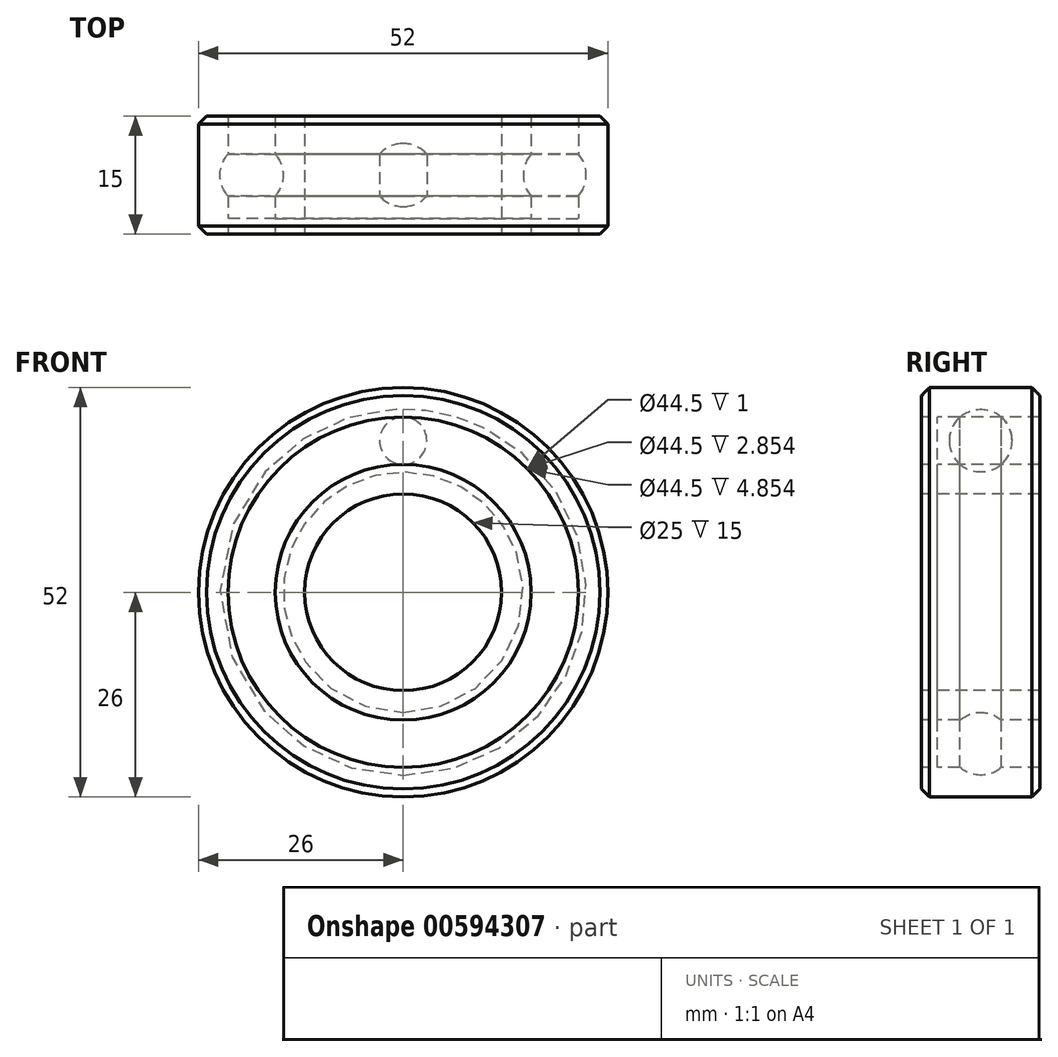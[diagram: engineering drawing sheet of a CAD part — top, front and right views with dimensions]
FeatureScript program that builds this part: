
annotation { "Feature Type Name" : "Feature", "Feature Type Description" : "" }
export const myFeature = defineFeature(function(context is Context, id is Id, definition is map)
    precondition{}
    {
        {
            var Q0;
            Q0=qCreatedBy(makeId("Right.planeOp"),FACE);
            var sketch = newSketch(context, id + "F0", { "sketchPlane" : qUnion([Q0])});
            skLineSegment(sketch, "E0", {"start": v(-30, 0) * mm, "end": v(30, 0) * mm, "construction": true});
            skSolve(sketch);
        }
        {
            var Q0;
            Q0=qCreatedBy(makeId("Right.planeOp"),FACE);
            var sketch = newSketch(context, id + "F1", { "sketchPlane" : qUnion([Q0])});
            skLineSegment(sketch, "E1.bottom", {"start": v(-7.5, 26) * mm, "end": v(7.5, 26) * mm});
            skLineSegment(sketch, "E1.top", {"start": v(-7.5, 12.5) * mm, "end": v(7.5, 12.5) * mm});
            skLineSegment(sketch, "E1.left", {"start": v(-7.5, 26) * mm, "end": v(-7.5, 12.5) * mm});
            skLineSegment(sketch, "E1.right", {"start": v(7.5, 26) * mm, "end": v(7.5, 12.5) * mm});
            skLineSegment(sketch, "E2", {"start": v(-11.72, 19.25) * mm, "end": v(12.7, 19.25) * mm, "construction": true});
            skCircle(sketch, "E3", {"center": v(0, 19.25) * mm, "radius": 4 * mm});
            skLineSegment(sketch, "E4", {"start": v(-7.5, 22.25) * mm, "end": v(7.5, 22.25) * mm});
            skLineSegment(sketch, "E5", {"start": v(-7.5, 16.25) * mm, "end": v(7.5, 16.25) * mm});
            skLineSegment(sketch, "E6.bottom", {"start": v(-6.5, 23.25) * mm, "end": v(-5.5, 23.25) * mm});
            skLineSegment(sketch, "E6.top", {"start": v(-6.5, 15.25) * mm, "end": v(-5.5, 15.25) * mm});
            skLineSegment(sketch, "E6.left", {"start": v(-6.5, 23.25) * mm, "end": v(-6.5, 15.25) * mm});
            skLineSegment(sketch, "E6.right", {"start": v(-5.5, 23.25) * mm, "end": v(-5.5, 15.25) * mm});
            skLineSegment(sketch, "E7", {"start": v(-4, 19.25) * mm, "end": v(4, 19.25) * mm});
            skSolve(sketch);
        }
        {
            var Q0;
            {var subQ5=sQuery(id+"F1.wireOp",EDGE,"E1.bottom");Q0=makeQuery(id+"F1.imprint","IMPRINT",FACE,{"disambiguationData":[TD([[makeQuery(id+"F1.imprint","IMPRINT",EDGE,{"derivedFrom":subQ5}),-1.0]])]});}
            var Q1;
            {var subQ4=sQuery(id+"F1.wireOp",EDGE,"E1.top");Q1=makeQuery(id+"F1.imprint","IMPRINT",FACE,{"disambiguationData":[TD([[makeQuery(id+"F1.imprint","IMPRINT",EDGE,{"derivedFrom":subQ4}),1.0]])]});}
            var Q2;
            Q2=sQuery(id+"F0.wireOp",EDGE,"E0");
            revolve(context, id + "F2", {"entities" : qUnion([Q0, Q1]), "axis" : qUnion([Q2]), "revolveType" : RevolveType.FULL});
        }
        {
            var Q0;
            Q0=makeQuery(id+"F2.opRevolve","SWEPT_EDGE",EDGE,{"disambiguationData":[OSD([sQuery(id+"F1.wireOp",EDGE,"E1.bottom"),sQuery(id+"F1.wireOp",EDGE,"E1.right")])]});
            var Q1;
            Q1=makeQuery(id+"F2.opRevolve","SWEPT_EDGE",EDGE,{"disambiguationData":[OSD([sQuery(id+"F1.wireOp",EDGE,"E1.bottom"),sQuery(id+"F1.wireOp",EDGE,"E1.left")])]});
            chamfer(context, id + "F3", {"entities" : qUnion([Q0, Q1]), "width" : 1 * mm, "tangentPropagation" : true});
        }
        {
            var Q0;
            {var subQ0=sQuery(id+"F1.wireOp",EDGE,"E7");Q0=makeQuery(id+"F1.imprint","IMPRINT",FACE,{"disambiguationData":[TD([[makeQuery(id+"F1.imprint","IMPRINT",EDGE,{"derivedFrom":subQ0}),1.0]])]});}
            var Q1;
            {var subQ0=sQuery(id+"F1.wireOp",EDGE,"E4");var subQ1=sQuery(id+"F1.wireOp",EDGE,"E3");var subQ2=makeQuery(id+"F1.imprint","INTERSECT",VERTEX,{"disambiguationData":[OD(0.0)],"derivedFrom":[subQ1,subQ0]});Q1=makeQuery(id+"F1.imprint","IMPRINT",FACE,{"disambiguationData":[TD([[makeQuery(id+"F1.imprint","IMPRINT",EDGE,{"disambiguationData":[TD([[subQ2,-1.0]])],"derivedFrom":subQ1}),1.0]])]});}
            var Q2;
            Q2=sQuery(id+"F1.wireOp",EDGE,"E2");
            revolve(context, id + "F4", {"operationType" : NewBodyOperationType.ADD, "entities" : qUnion([Q0, Q1]), "axis" : qUnion([Q2]), "revolveType" : RevolveType.FULL});
        }
        {
            var Q0;
            {var subQ5=sQuery(id+"F1.wireOp",EDGE,"E6.bottom");Q0=makeQuery(id+"F1.imprint","IMPRINT",FACE,{"disambiguationData":[TD([[makeQuery(id+"F1.imprint","IMPRINT",EDGE,{"derivedFrom":subQ5}),-1.0]])]});}
            var Q1;
            {var subQ0=sQuery(id+"F1.wireOp",EDGE,"E6.left");var subQ1=sQuery(id+"F1.wireOp",EDGE,"E4");var subQ2=makeQuery(id+"F1.imprint","INTERSECT",VERTEX,{"derivedFrom":[subQ1,subQ0]});Q1=makeQuery(id+"F1.imprint","IMPRINT",FACE,{"disambiguationData":[TD([[makeQuery(id+"F1.imprint","IMPRINT",EDGE,{"disambiguationData":[TD([[subQ2,-1.0]])],"derivedFrom":subQ1}),-1.0]])]});}
            var Q2;
            {var subQ5=sQuery(id+"F1.wireOp",EDGE,"E6.top");Q2=makeQuery(id+"F1.imprint","IMPRINT",FACE,{"disambiguationData":[TD([[makeQuery(id+"F1.imprint","IMPRINT",EDGE,{"derivedFrom":subQ5}),1.0]])]});}
            var Q3;
            Q3=sQuery(id+"F0.wireOp",EDGE,"E0");
            revolve(context, id + "F5", {"operationType" : NewBodyOperationType.ADD, "entities" : qUnion([Q0, Q1, Q2]), "axis" : qUnion([Q3]), "revolveType" : RevolveType.FULL});
        }
        {
            var Q0;
            Q0=makeQuery(id+"F2.opRevolve","SWEPT_BODY",BODY,{"disambiguationData":[OSD([sQuery(id+"F1.wireOp",EDGE,"E1.bottom"),sQuery(id+"F1.wireOp",EDGE,"E1.left"),sQuery(id+"F1.wireOp",EDGE,"E1.right"),sQuery(id+"F1.wireOp",EDGE,"E3"),sQuery(id+"F1.wireOp",EDGE,"E4"),sQuery(id+"F1.wireOp",EDGE,"E6.bottom"),sQuery(id+"F1.wireOp",EDGE,"E6.left"),sQuery(id+"F1.wireOp",EDGE,"E6.right")])]});
            var Q1;
            Q1=makeQuery(id+"F2.opRevolve","SWEPT_BODY",BODY,{"disambiguationData":[OSD([sQuery(id+"F1.wireOp",EDGE,"E1.top"),sQuery(id+"F1.wireOp",EDGE,"E1.left"),sQuery(id+"F1.wireOp",EDGE,"E1.right"),sQuery(id+"F1.wireOp",EDGE,"E3"),sQuery(id+"F1.wireOp",EDGE,"E5"),sQuery(id+"F1.wireOp",EDGE,"E6.top"),sQuery(id+"F1.wireOp",EDGE,"E6.left"),sQuery(id+"F1.wireOp",EDGE,"E6.right")])]});
            var Q2;
            Q2=makeQuery(id+"FPRDvoFmUIFufR5_3.10.F4.opRevolve","SWEPT_BODY",BODY,{"disambiguationData":[OSD([sQuery(id+"F1.wireOp",EDGE,"E3"),sQuery(id+"F1.wireOp",EDGE,"E7")])]});
            var Q3;
            Q3=makeQuery(id+"FPRDvoFmUIFufR5_3.11.F4.opRevolve","SWEPT_BODY",BODY,{"disambiguationData":[OSD([sQuery(id+"F1.wireOp",EDGE,"E3"),sQuery(id+"F1.wireOp",EDGE,"E7")])]});
            var Q4;
            Q4=makeQuery(id+"FPRDvoFmUIFufR5_3.6.F4.opRevolve","SWEPT_BODY",BODY,{"disambiguationData":[OSD([sQuery(id+"F1.wireOp",EDGE,"E3"),sQuery(id+"F1.wireOp",EDGE,"E7")])]});
            var Q5;
            Q5=makeQuery(id+"FPRDvoFmUIFufR5_3.7.F4.opRevolve","SWEPT_BODY",BODY,{"disambiguationData":[OSD([sQuery(id+"F1.wireOp",EDGE,"E3"),sQuery(id+"F1.wireOp",EDGE,"E7")])]});
            var Q6;
            Q6=makeQuery(id+"FPRDvoFmUIFufR5_3.8.F4.opRevolve","SWEPT_BODY",BODY,{"disambiguationData":[OSD([sQuery(id+"F1.wireOp",EDGE,"E3"),sQuery(id+"F1.wireOp",EDGE,"E7")])]});
            var Q7;
            Q7=makeQuery(id+"FPRDvoFmUIFufR5_3.4.F4.opRevolve","SWEPT_BODY",BODY,{"disambiguationData":[OSD([sQuery(id+"F1.wireOp",EDGE,"E3"),sQuery(id+"F1.wireOp",EDGE,"E7")])]});
            var Q8;
            Q8=makeQuery(id+"FPRDvoFmUIFufR5_3.2.F4.opRevolve","SWEPT_BODY",BODY,{"disambiguationData":[OSD([sQuery(id+"F1.wireOp",EDGE,"E3"),sQuery(id+"F1.wireOp",EDGE,"E7")])]});
            var Q9;
            Q9=makeQuery(id+"F4.opRevolve","SWEPT_BODY",BODY,{"disambiguationData":[OSD([sQuery(id+"F1.wireOp",EDGE,"E3"),sQuery(id+"F1.wireOp",EDGE,"E7")])]});
            var Q10;
            Q10=makeQuery(id+"FPRDvoFmUIFufR5_3.5.F4.opRevolve","SWEPT_BODY",BODY,{"disambiguationData":[OSD([sQuery(id+"F1.wireOp",EDGE,"E3"),sQuery(id+"F1.wireOp",EDGE,"E7")])]});
            var Q11;
            Q11=makeQuery(id+"FPRDvoFmUIFufR5_3.3.F4.opRevolve","SWEPT_BODY",BODY,{"disambiguationData":[OSD([sQuery(id+"F1.wireOp",EDGE,"E3"),sQuery(id+"F1.wireOp",EDGE,"E7")])]});
            var Q12;
            Q12=makeQuery(id+"FPRDvoFmUIFufR5_3.1.F4.opRevolve","SWEPT_BODY",BODY,{"disambiguationData":[OSD([sQuery(id+"F1.wireOp",EDGE,"E3"),sQuery(id+"F1.wireOp",EDGE,"E7")])]});
            var Q13;
            Q13=makeQuery(id+"FPRDvoFmUIFufR5_3.9.F4.opRevolve","SWEPT_BODY",BODY,{"disambiguationData":[OSD([sQuery(id+"F1.wireOp",EDGE,"E3"),sQuery(id+"F1.wireOp",EDGE,"E7")])]});
            booleanBodies(context, id + "F6", {"operationType" : BooleanOperationType.UNION, "tools" : qUnion([Q0, Q1, Q2, Q3, Q4, Q5, Q6, Q7, Q8, Q9, Q10, Q11, Q12, Q13])});
        }
    });
